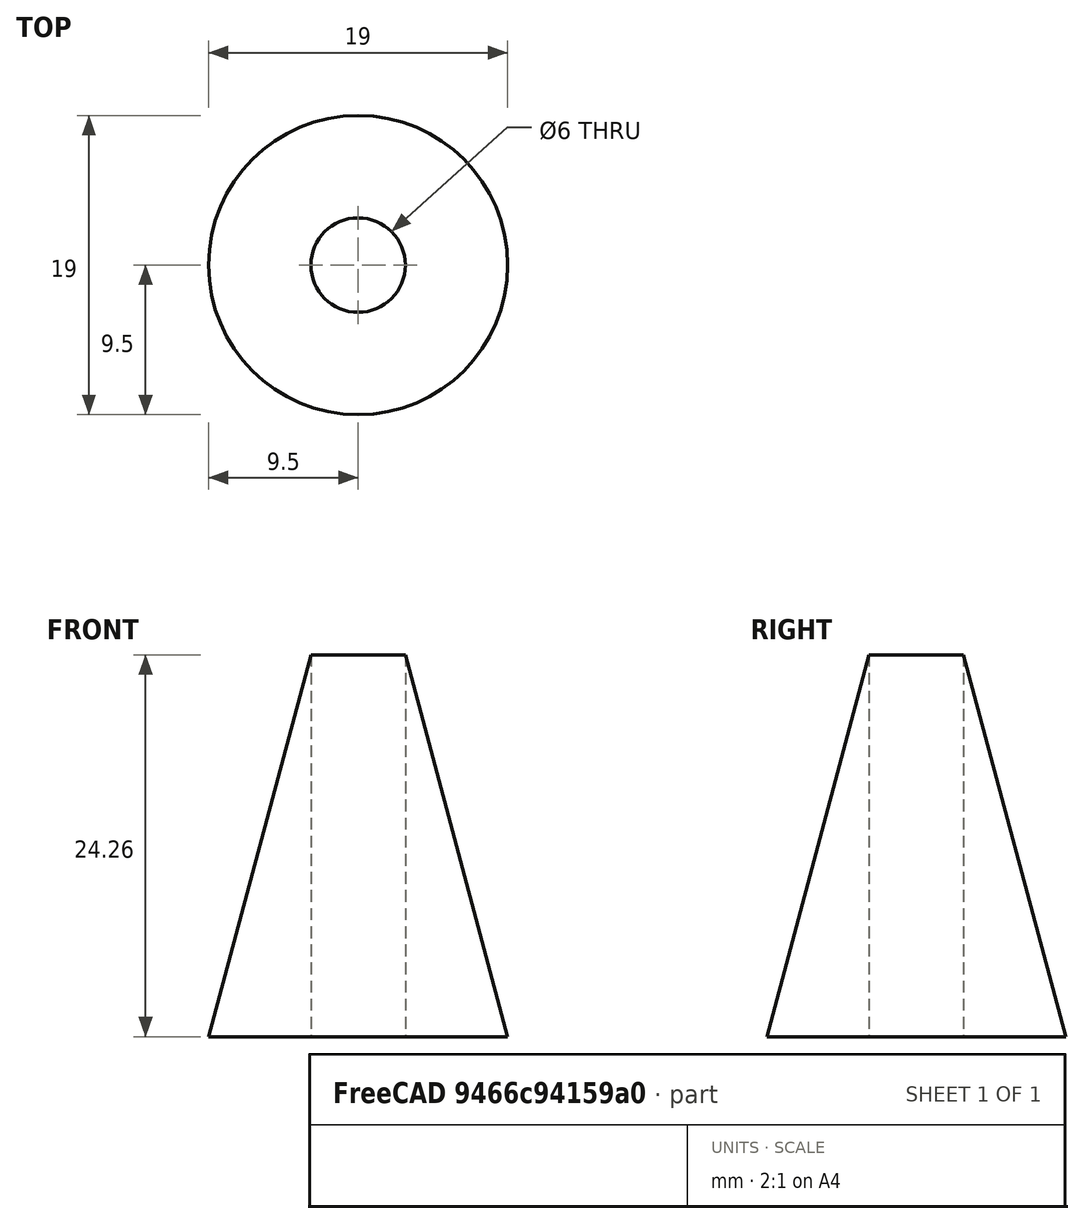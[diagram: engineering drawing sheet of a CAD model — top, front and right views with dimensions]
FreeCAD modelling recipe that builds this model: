
FCSTD DOCUMENT  (FreeCAD 0.19R24291 (Git))
Label: windDirectionArrowTop
License: All rights reserved
LicenseURL: http://en.wikipedia.org/wiki/All_rights_reserved
objects: Sketcher::SketchObject×1, PartDesign::Revolution×1, PartDesign::Body×1
note: 4 computed .brp shape members not serialized (recipe doc carries the construction recipe); baked Part::Feature solids carry a one-line shape summary decoded from their .brp

FEATURE [Sketcher::SketchObject] Sketch
  FullyConstrained = true
  MapMode = 5
  Placement = pos=(0,0,0) rot=(1,0,0;1.5708rad)
  Support = -> [XZ_Plane]
  sketch-geometry (3):
    g0: LineSegment StartX=3 StartY=0 StartZ=0 EndX=9.5 EndY=0 EndZ=0
    g1: LineSegment StartX=9.5 StartY=0 StartZ=0 EndX=3 EndY=24.2583 EndZ=0
    g2: LineSegment StartX=3 StartY=24.2583 StartZ=0 EndX=3 EndY=0 EndZ=0
  constraints (9):
    c: PointOnObject(g0,g-1)
    c: Horizontal(g0)
    c: Coincident(g1,g0)
    c: Coincident(g2,g1)
    c: Coincident(g2,g0)
    c: Vertical(g2)
    c: DistanceX(g-1,g0) = 3
    c: Angle(g1,g0) = 1.309
    c: DistanceX(g0,g0) = 6.5
FEATURE [PartDesign::Revolution] Revolution
  Angle = 360
  Axis = (0,2e-16,1)
  Base = (0,0,0)
  Placement = pos=(0,0,0) rot=(1,0,0;1.5708rad)
  Profile = -> Sketch
  ReferenceAxis = -> Sketch [V_Axis]
  Reversed = true
FEATURE [PartDesign::Body] Body
  Group = -> [Sketch,Revolution]
  Origin = -> Origin
  Tip = -> Revolution
